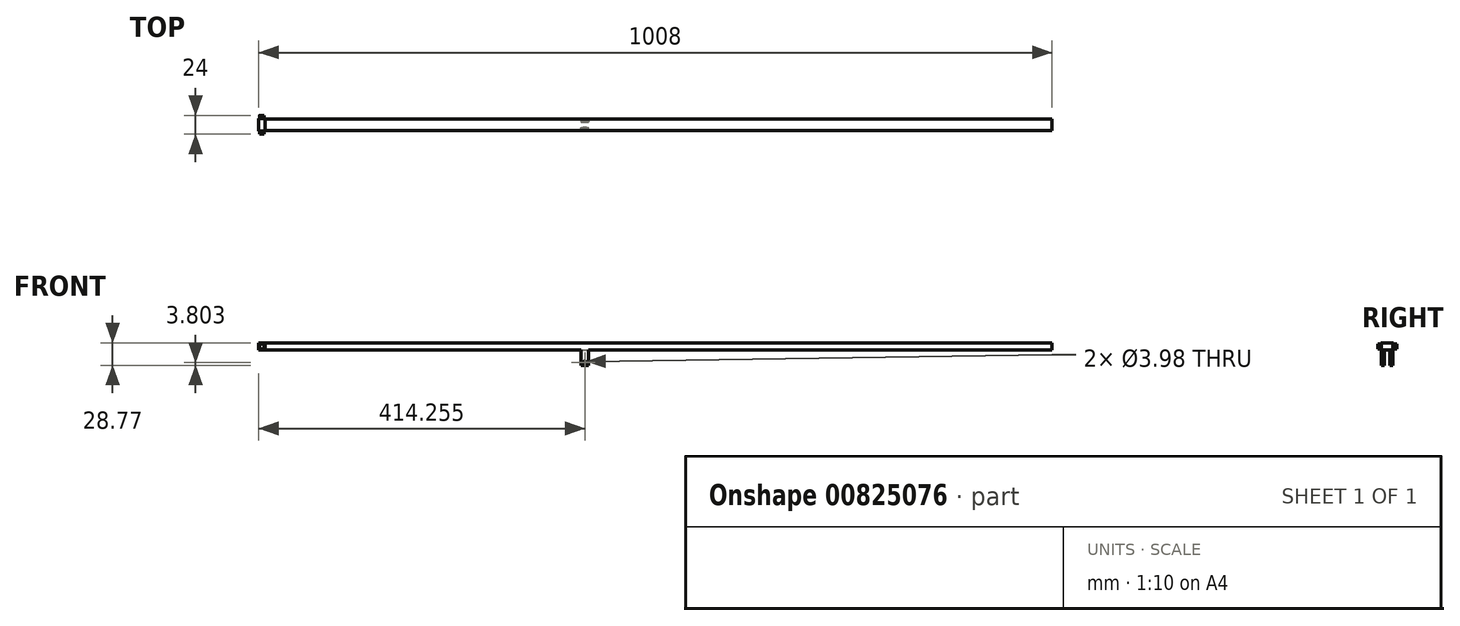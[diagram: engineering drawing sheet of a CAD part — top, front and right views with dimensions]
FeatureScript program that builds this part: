
annotation { "Feature Type Name" : "Feature", "Feature Type Description" : "" }
export const myFeature = defineFeature(function(context is Context, id is Id, definition is map)
    precondition{}
    {
        {
            var Q0;
            Q0=qCreatedBy(makeId("Right.planeOp"),FACE);
            var sketch = newSketch(context, id + "F0", { "sketchPlane" : qUnion([Q0])});
            skLineSegment(sketch, "E0.bottom", {"start": v(-12, 4.5) * mm, "end": v(12, 4.5) * mm});
            skLineSegment(sketch, "E0.top", {"start": v(-12, -4.5) * mm, "end": v(12, -4.5) * mm});
            skLineSegment(sketch, "E0.left", {"start": v(-12, 4.5) * mm, "end": v(-12, -4.5) * mm});
            skLineSegment(sketch, "E0.right", {"start": v(12, 4.5) * mm, "end": v(12, -4.5) * mm});
            skPoint(sketch, "E0.middle", {"position": v(0, 0) * mm});
            skSolve(sketch);
        }
        {
            var Q0;
            Q0=makeQuery(id+"F0.imprint","IMPRINT",FACE,{"disambiguationData":[TD([[makeQuery(id+"F0.imprint","IMPRINT",EDGE,{"derivedFrom":sQuery(id+"F0.wireOp",EDGE,"E0.bottom")}),-1.0]])]});
            extrude(context, id + "F1", {"entities" : qUnion([Q0]), "endBound" : BoundingType.SYMMETRIC, "depth" : 8 * mm, "offsetDistance" : 25 * mm});
        }
        {
            var Q0;
            Q0=makeQuery(id+"F1.opExtrude","SWEPT_FACE",FACE,{"disambiguationData":[OSD([sQuery(id+"F0.wireOp",EDGE,"E0.left")])]});
            var sketch = newSketch(context, id + "F2", { "sketchPlane" : qUnion([Q0])});
            skCircle(sketch, "E1", {"center": v(0, 0) * mm, "radius": 3 * mm});
            skSolve(sketch);
        }
        {
            var Q0;
            Q0=makeQuery(id+"F2.imprint","IMPRINT",FACE,{"disambiguationData":[TD([[makeQuery(id+"F2.imprint","IMPRINT",EDGE,{"derivedFrom":sQuery(id+"F2.wireOp",EDGE,"E1")}),-1.0]])]});
            extrude(context, id + "F3", {"entities" : qUnion([Q0]), "operationType" : NewBodyOperationType.REMOVE, "oppositeDirection" : true, "depth" : 4 * mm, "offsetDistance" : 25 * mm});
        }
        {
            var Q0;
            Q0=makeQuery(id+"F1.opExtrude","SWEPT_FACE",FACE,{"disambiguationData":[OSD([sQuery(id+"F0.wireOp",EDGE,"E0.right")])]});
            var sketch = newSketch(context, id + "F4", { "sketchPlane" : qUnion([Q0])});
            skCircle(sketch, "E2", {"center": v(0, 0) * mm, "radius": 3 * mm});
            skSolve(sketch);
        }
        {
            var Q0;
            Q0=makeQuery(id+"F4.imprint","IMPRINT",FACE,{"disambiguationData":[TD([[makeQuery(id+"F4.imprint","IMPRINT",EDGE,{"derivedFrom":sQuery(id+"F4.wireOp",EDGE,"E2")}),-1.0]])]});
            extrude(context, id + "F5", {"entities" : qUnion([Q0]), "operationType" : NewBodyOperationType.REMOVE, "oppositeDirection" : true, "depth" : 4 * mm, "offsetDistance" : 25 * mm});
        }
        {
            var Q0;
            Q0=makeQuery(id+"F1.opExtrude","CAP_FACE",FACE,{"disambiguationData":[OSD([sQuery(id+"F0.wireOp",EDGE,"E0.bottom"),sQuery(id+"F0.wireOp",EDGE,"E0.top"),sQuery(id+"F0.wireOp",EDGE,"E0.left"),sQuery(id+"F0.wireOp",EDGE,"E0.right")])],"isStart":false});
            var sketch = newSketch(context, id + "F6", { "sketchPlane" : qUnion([Q0])});
            skLineSegment(sketch, "E3.bottom", {"start": v(-7.38, 4.27) * mm, "end": v(7.38, 4.27) * mm});
            skLineSegment(sketch, "E3.top", {"start": v(-7.38, -4.27) * mm, "end": v(7.38, -4.27) * mm});
            skLineSegment(sketch, "E3.left", {"start": v(-7.38, 4.27) * mm, "end": v(-7.38, -4.27) * mm});
            skLineSegment(sketch, "E3.right", {"start": v(7.38, 4.27) * mm, "end": v(7.38, -4.27) * mm});
            skPoint(sketch, "E3.middle", {"position": v(0, 0) * mm});
            skSolve(sketch);
        }
        {
            var Q0;
            Q0=makeQuery(id+"F6.imprint","IMPRINT",FACE,{"disambiguationData":[TD([[makeQuery(id+"F6.imprint","IMPRINT",EDGE,{"derivedFrom":sQuery(id+"F6.wireOp",EDGE,"E3.bottom")}),-1.0]])]});
            extrude(context, id + "F7", {"entities" : qUnion([Q0]), "operationType" : NewBodyOperationType.ADD, "depth" : 1000 * mm, "offsetDistance" : 25 * mm});
        }
        {
            var Q0;
            Q0=makeQuery(id+"F7.opExtrude","SWEPT_FACE",FACE,{"disambiguationData":[OSD([sQuery(id+"F6.wireOp",EDGE,"E3.top")])]});
            var sketch = newSketch(context, id + "F8", { "sketchPlane" : qUnion([Q0])});
            skLineSegment(sketch, "E4.bottom", {"start": v(405.25, 7.38) * mm, "end": v(415.25, 7.38) * mm});
            skLineSegment(sketch, "E4.top", {"start": v(405.25, 3.38) * mm, "end": v(415.25, 3.38) * mm});
            skLineSegment(sketch, "E4.left", {"start": v(405.25, 7.38) * mm, "end": v(405.25, 3.38) * mm});
            skLineSegment(sketch, "E4.right", {"start": v(415.25, 7.38) * mm, "end": v(415.25, 3.38) * mm});
            skLineSegment(sketch, "E5.MirrorCS", {"start": v(405.25, -3.38) * mm, "end": v(415.25, -3.38) * mm});
            skLineSegment(sketch, "E6.MirrorCS", {"start": v(405.25, -7.38) * mm, "end": v(415.25, -7.38) * mm});
            skLineSegment(sketch, "E7.MirrorCS", {"start": v(405.25, -7.38) * mm, "end": v(405.25, -3.38) * mm});
            skLineSegment(sketch, "E8.MirrorCS", {"start": v(415.25, -7.38) * mm, "end": v(415.25, -3.38) * mm});
            skSolve(sketch);
        }
        {
            var Q0;
            Q0=makeQuery(id+"F8.imprint","IMPRINT",FACE,{"disambiguationData":[TD([[makeQuery(id+"F8.imprint","IMPRINT",EDGE,{"derivedFrom":sQuery(id+"F8.wireOp",EDGE,"E4.bottom")}),1.0]])]});
            extrude(context, id + "F9", {"entities" : qUnion([Q0]), "operationType" : NewBodyOperationType.ADD, "depth" : 20 * mm, "offsetDistance" : 25 * mm});
        }
        {
            var Q0;
            Q0=makeQuery(id+"F8.imprint","IMPRINT",FACE,{"disambiguationData":[TD([[makeQuery(id+"F8.imprint","IMPRINT",EDGE,{"derivedFrom":sQuery(id+"F8.wireOp",EDGE,"E5.MirrorCS")}),-1.0]])]});
            extrude(context, id + "F10", {"entities" : qUnion([Q0]), "operationType" : NewBodyOperationType.ADD, "depth" : 20 * mm, "offsetDistance" : 25 * mm});
        }
        {
            var Q0;
            Q0=makeQuery(id+"F9.boolean.opBoolean","MERGE",FACE,{"derivedFrom":[makeQuery(id+"F7.opExtrude","SWEPT_FACE",FACE,{"disambiguationData":[OSD([sQuery(id+"F6.wireOp",EDGE,"E3.left")])]}),makeQuery(id+"F9.opExtrude","SWEPT_FACE",FACE,{"disambiguationData":[OSD([sQuery(id+"F8.wireOp",EDGE,"E4.bottom")])]})]});
            var sketch = newSketch(context, id + "F11", { "sketchPlane" : qUnion([Q0])});
            skCircle(sketch, "E9", {"center": v(410.25, -20.47) * mm, "radius": 2 * mm});
            skPoint(sketch, "E9.centerSnap0", {"position": v(410.25, -24.27) * mm});
            skSolve(sketch);
        }
        {
            var Q0;
            Q0=makeQuery(id+"F11.imprint","IMPRINT",FACE,{"disambiguationData":[TD([[makeQuery(id+"F11.imprint","IMPRINT",EDGE,{"derivedFrom":sQuery(id+"F11.wireOp",EDGE,"E9")}),1.0]])]});
            extrude(context, id + "F12", {"entities" : qUnion([Q0]), "operationType" : NewBodyOperationType.REMOVE, "oppositeDirection" : true, "depth" : 50 * mm, "offsetDistance" : 25 * mm});
        }
    });
